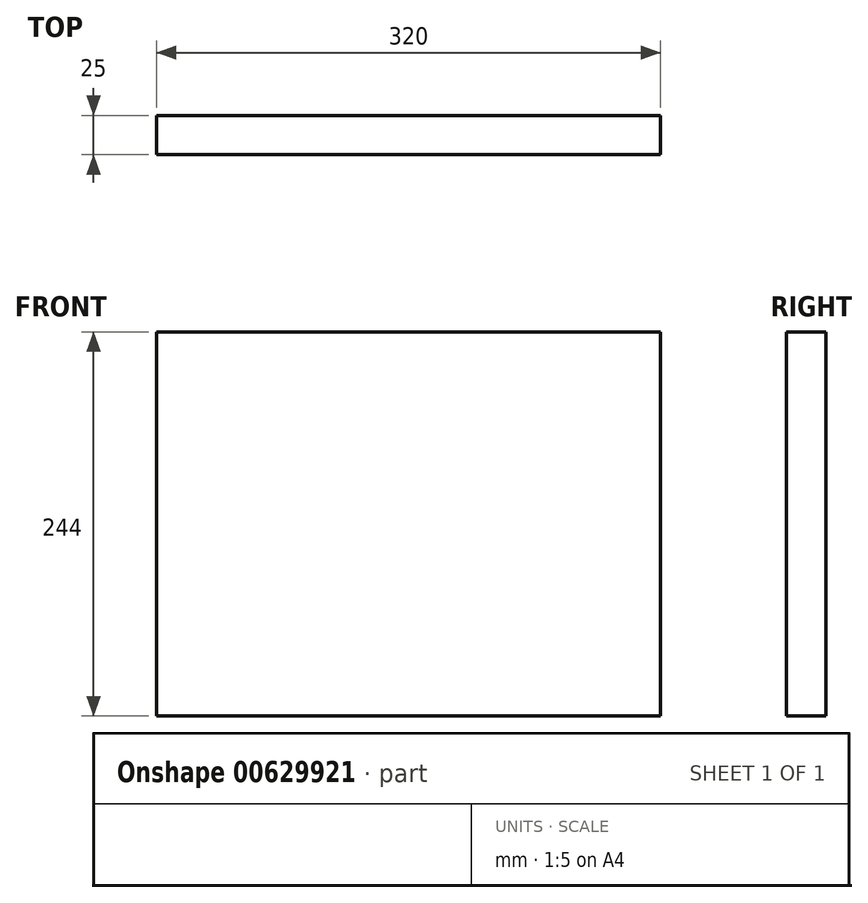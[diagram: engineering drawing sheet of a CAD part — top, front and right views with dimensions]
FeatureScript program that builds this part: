
annotation { "Feature Type Name" : "Feature", "Feature Type Description" : "" }
export const myFeature = defineFeature(function(context is Context, id is Id, definition is map)
    precondition{}
    {
        {
            var Q0;
            Q0=qCreatedBy(makeId("Front.planeOp"),FACE);
            var sketch = newSketch(context, id + "F0", { "sketchPlane" : qUnion([Q0])});
            skLineSegment(sketch, "E0.bottom", {"start": v(0, 0) * mm, "end": v(320, 0) * mm});
            skLineSegment(sketch, "E0.top", {"start": v(0, 244) * mm, "end": v(320, 244) * mm});
            skLineSegment(sketch, "E0.left", {"start": v(0, 0) * mm, "end": v(0, 244) * mm});
            skLineSegment(sketch, "E0.right", {"start": v(320, 0) * mm, "end": v(320, 244) * mm});
            skSolve(sketch);
        }
        {
            var Q0;
            Q0=makeQuery(id+"F0.imprint","IMPRINT",FACE,{"disambiguationData":[TD([[makeQuery(id+"F0.imprint","IMPRINT",EDGE,{"derivedFrom":sQuery(id+"F0.wireOp",EDGE,"E0.bottom")}),1.0]])]});
            extrude(context, id + "F1", {"entities" : qUnion([Q0]), "depth" : 25 * mm, "offsetDistance" : 25 * mm});
        }
    });
